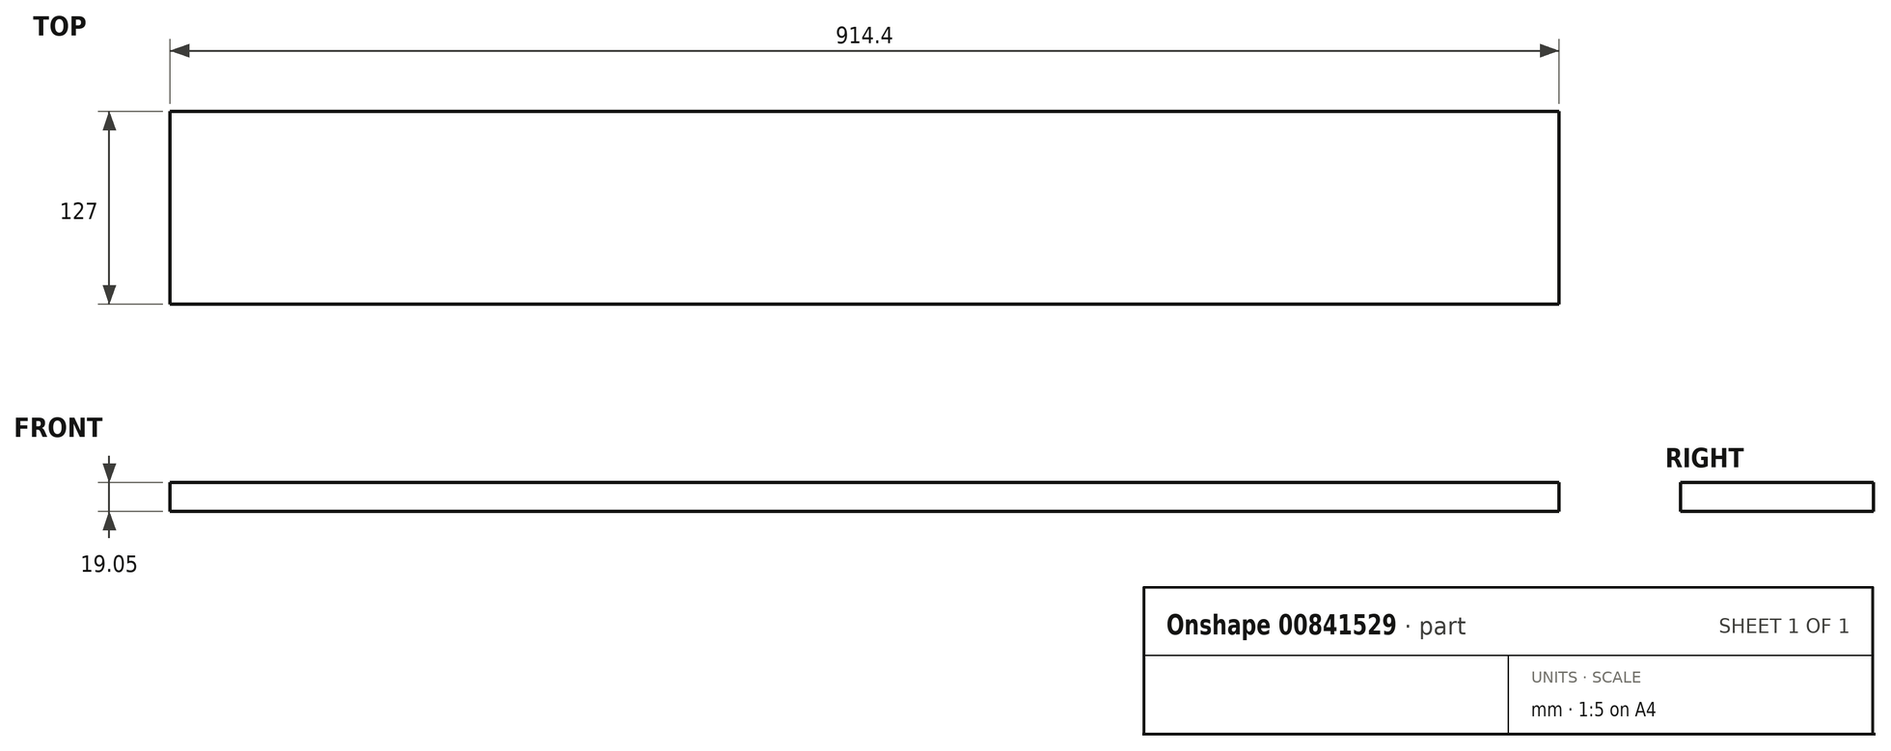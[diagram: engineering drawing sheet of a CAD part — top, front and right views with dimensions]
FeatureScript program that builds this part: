
annotation { "Feature Type Name" : "Feature", "Feature Type Description" : "" }
export const myFeature = defineFeature(function(context is Context, id is Id, definition is map)
    precondition{}
    {
        {
            var Q0;
            Q0=qCreatedBy(makeId("Top.planeOp"),FACE);
            var sketch = newSketch(context, id + "F0", { "sketchPlane" : qUnion([Q0])});
            skLineSegment(sketch, "E0.bottom", {"start": v(-457.2, 0) * mm, "end": v(457.2, 0) * mm});
            skLineSegment(sketch, "E0.top", {"start": v(-457.2, 127) * mm, "end": v(457.2, 127) * mm});
            skLineSegment(sketch, "E0.left", {"start": v(-457.2, 0) * mm, "end": v(-457.2, 127) * mm});
            skLineSegment(sketch, "E0.right", {"start": v(457.2, 0) * mm, "end": v(457.2, 127) * mm});
            skSolve(sketch);
        }
        {
            var Q0;
            Q0=qSketchRegion(id+"F0",true);
            extrude(context, id + "F1", {"entities" : qUnion([Q0]), "depth" : 19.05 * mm, "offsetDistance" : 25.4 * mm});
        }
    });
